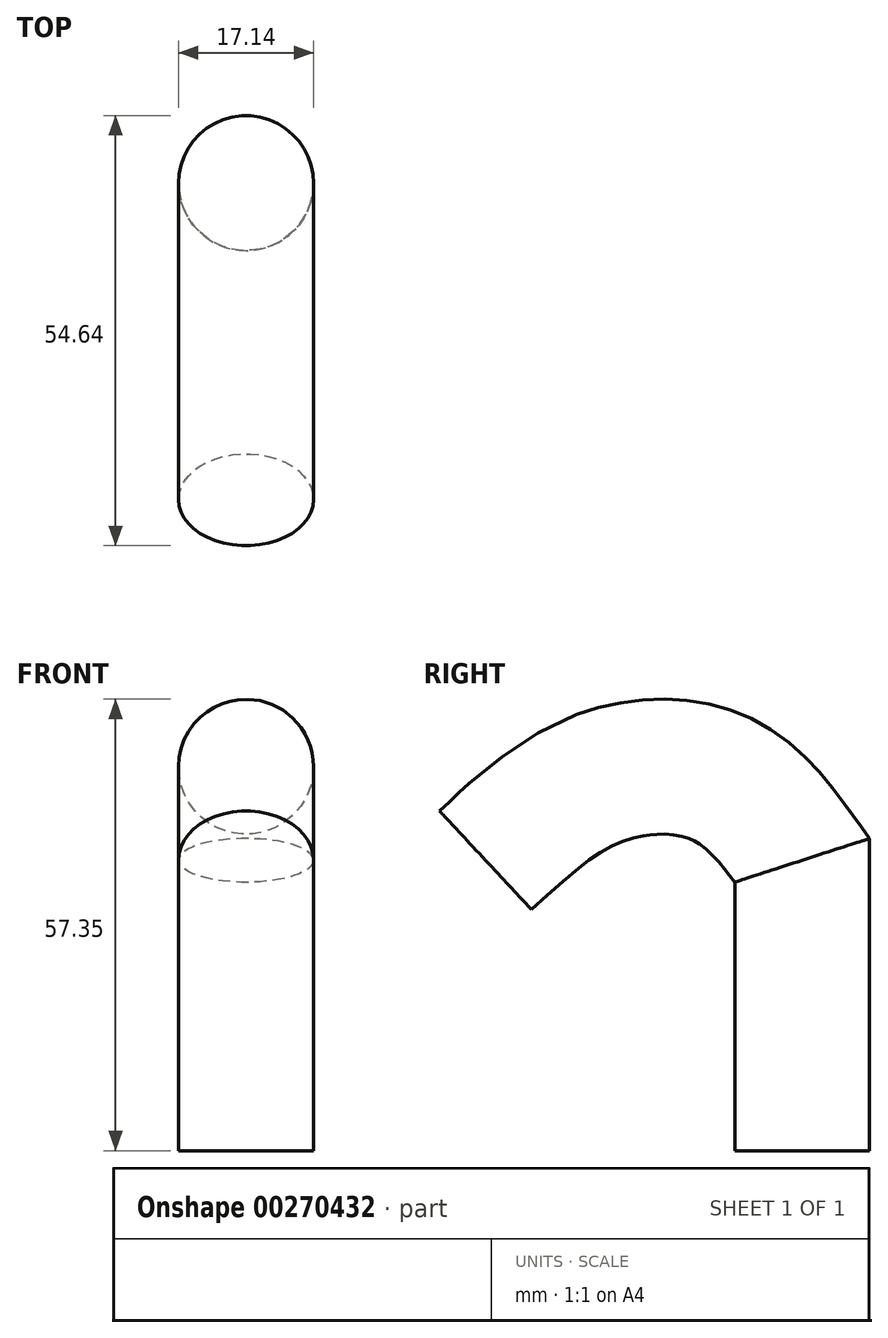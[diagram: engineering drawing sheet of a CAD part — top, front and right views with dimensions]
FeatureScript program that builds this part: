
annotation { "Feature Type Name" : "Feature", "Feature Type Description" : "" }
export const myFeature = defineFeature(function(context is Context, id is Id, definition is map)
    precondition{}
    {
        {
            var Q0;
            Q0=qCreatedBy(makeId("Right.planeOp"),FACE);
            var sketch = newSketch(context, id + "F0", { "sketchPlane" : qUnion([Q0])});
            skLineSegment(sketch, "E0", {"start": v(0, 0) * mm, "end": v(0, 36.9) * mm});
            skFitSpline(sketch, "E1", {"points": [v(0, 36.9) * mm, v(-10.36, 47.26) * mm, v(-25.91, 47.26) * mm, v(-40.22, 36.9) * mm], "startDerivative": vector(-28.13, 39.05) * mm, "endDerivative": vector(-37.97, -35.38) * mm});
            skSolve(sketch);
        }
        {
            var Q0;
            Q0=qCreatedBy(makeId("Top.planeOp"),FACE);
            var sketch = newSketch(context, id + "F1", { "sketchPlane" : qUnion([Q0])});
            skCircle(sketch, "E2", {"center": v(0, 0) * mm, "radius": 8.57 * mm});
            skSolve(sketch);
        }
        {
            var Q0;
            Q0=makeQuery(id+"F1.imprint","IMPRINT",FACE,{"disambiguationData":[TD([[makeQuery(id+"F1.imprint","IMPRINT",EDGE,{"derivedFrom":sQuery(id+"F1.wireOp",EDGE,"E2")}),1.0]])]});
            var Q1;
            Q1=sQuery(id+"F0.wireOp",EDGE,"E0");
            var Q2;
            Q2=sQuery(id+"F0.wireOp",EDGE,"E1");
            sweep(context, id + "F2", {"profiles" : qUnion([Q0]), "path" : qUnion([Q1, Q2])});
        }
    });
